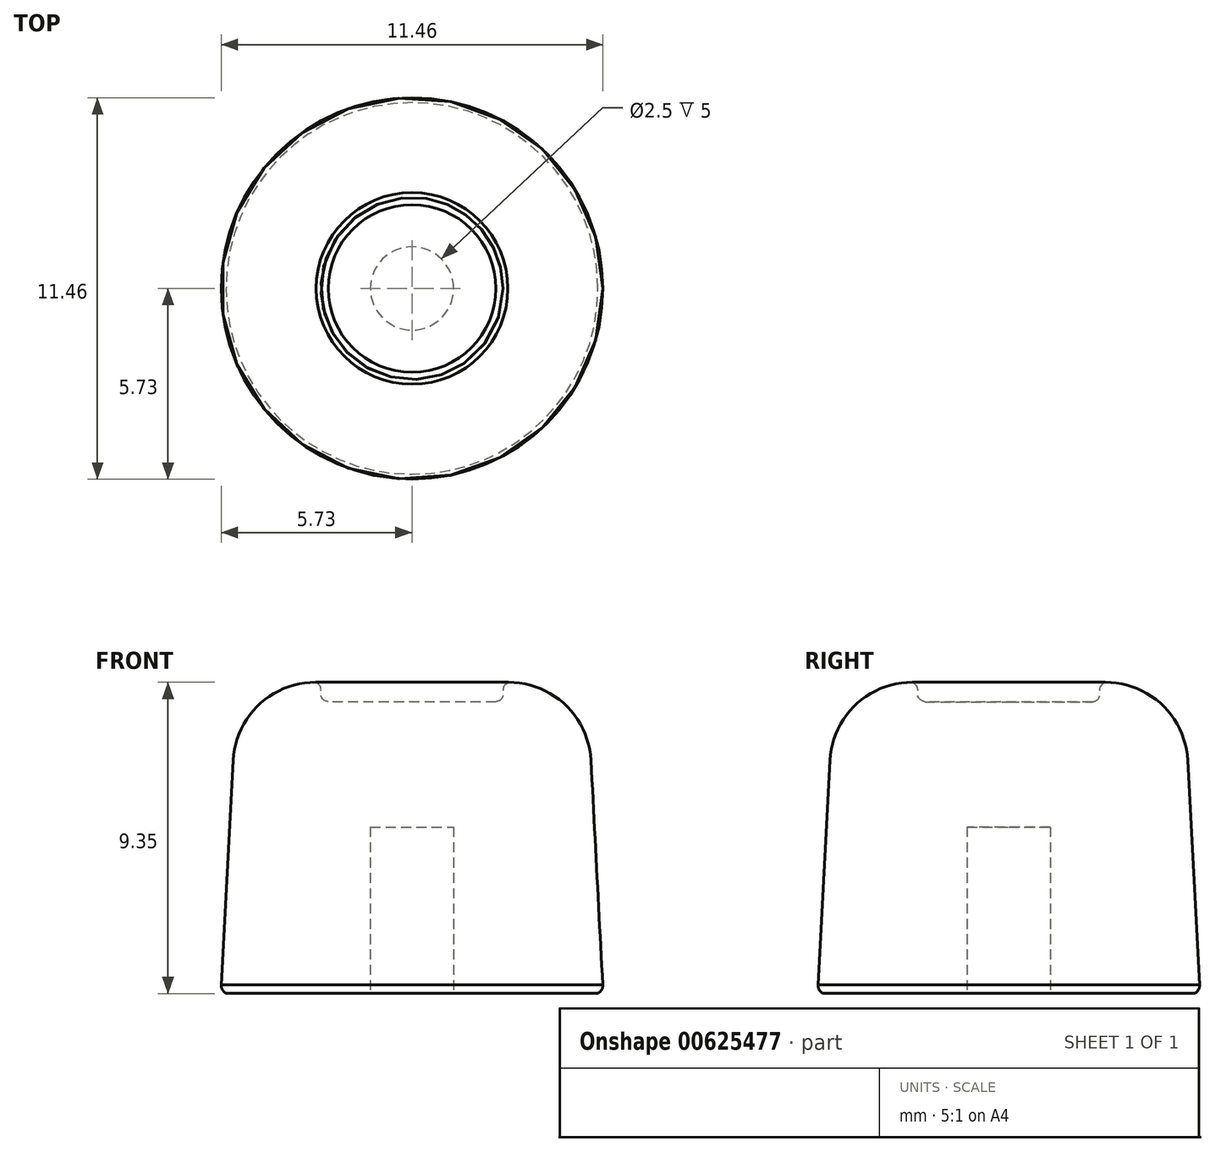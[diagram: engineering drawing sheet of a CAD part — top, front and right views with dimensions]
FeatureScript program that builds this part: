
annotation { "Feature Type Name" : "Feature", "Feature Type Description" : "" }
export const myFeature = defineFeature(function(context is Context, id is Id, definition is map)
    precondition{}
    {
        {
            var Q0;
            Q0=qCreatedBy(makeId("Top.planeOp"),FACE);
            var sketch = newSketch(context, id + "F0", { "sketchPlane" : qUnion([Q0])});
            skCircle(sketch, "E0", {"center": v(0, 0) * mm, "radius": 1.25 * mm});
            skSolve(sketch);
        }
        {
            var Q0;
            Q0=qCreatedBy(makeId("Right.planeOp"),FACE);
            var sketch = newSketch(context, id + "F1", { "sketchPlane" : qUnion([Q0])});
            skLineSegment(sketch, "E1", {"start": v(-5.73, -4.42) * mm, "end": v(-5.37, 2.33) * mm});
            skArc(sketch, "E2", {"start": v(-2.88, 4.67) * mm, "mid": v(-4.6, 4) * mm, "end": v(-5.37, 2.33) * mm});
            skFitSpline(sketch, "E3", {"points": [v(-2.88, 4.67) * mm, v(-2.75, 4.54) * mm, v(-2.74, 4.4) * mm, v(-2.72, 4.23) * mm, v(-2.64, 4.13) * mm, v(-2.57, 4.1) * mm, v(-2.52, 4.08) * mm], "startDerivative": vector(0.74, -0.63) * mm, "endDerivative": vector(0.48, -0.15) * mm});
            skLineSegment(sketch, "E4", {"start": v(-2.52, 4.08) * mm, "end": v(0, 4.08) * mm});
            skLineSegment(sketch, "E5", {"start": v(0, 4.08) * mm, "end": v(0, -4.68) * mm});
            skLineSegment(sketch, "E6", {"start": v(0, -4.68) * mm, "end": v(-5.58, -4.68) * mm});
            skFitSpline(sketch, "E7", {"points": [v(-5.73, -4.42) * mm, v(-5.73, -4.46) * mm, v(-5.71, -4.52) * mm, v(-5.69, -4.58) * mm, v(-5.65, -4.63) * mm, v(-5.58, -4.68) * mm], "startDerivative": vector(-0.01, -0.24) * mm, "endDerivative": vector(0.3, -0.21) * mm});
            skSolve(sketch);
        }
        {
            var Q0;
            Q0 = qSketchRegion(id + "F1", true);
            var Q1;
            Q1=sQuery(id+"F1.wireOp",EDGE,"E5");
            revolve(context, id + "F2", {"entities" : qUnion([Q0]), "axis" : qUnion([Q1]), "revolveType" : RevolveType.FULL});
        }
        {
            var Q0;
            Q0=makeQuery(id+"F2.opRevolve","SWEPT_FACE",FACE,{"disambiguationData":[OSD([sQuery(id+"F1.wireOp",EDGE,"E6")])]});
            var sketch = newSketch(context, id + "F3", { "sketchPlane" : qUnion([Q0])});
            skCircle(sketch, "E8", {"center": v(0, 0) * mm, "radius": 1.25 * mm});
            skSolve(sketch);
        }
        {
            var Q0;
            Q0=makeQuery(id+"F3.imprint","IMPRINT",FACE,{"disambiguationData":[TD([[makeQuery(id+"F3.imprint","IMPRINT",EDGE,{"derivedFrom":sQuery(id+"F3.wireOp",EDGE,"E8")}),1.0]])]});
            extrude(context, id + "F4", {"entities" : qUnion([Q0]), "operationType" : NewBodyOperationType.REMOVE, "oppositeDirection" : true, "depth" : 5 * mm, "offsetDistance" : 25 * mm});
        }
    });
